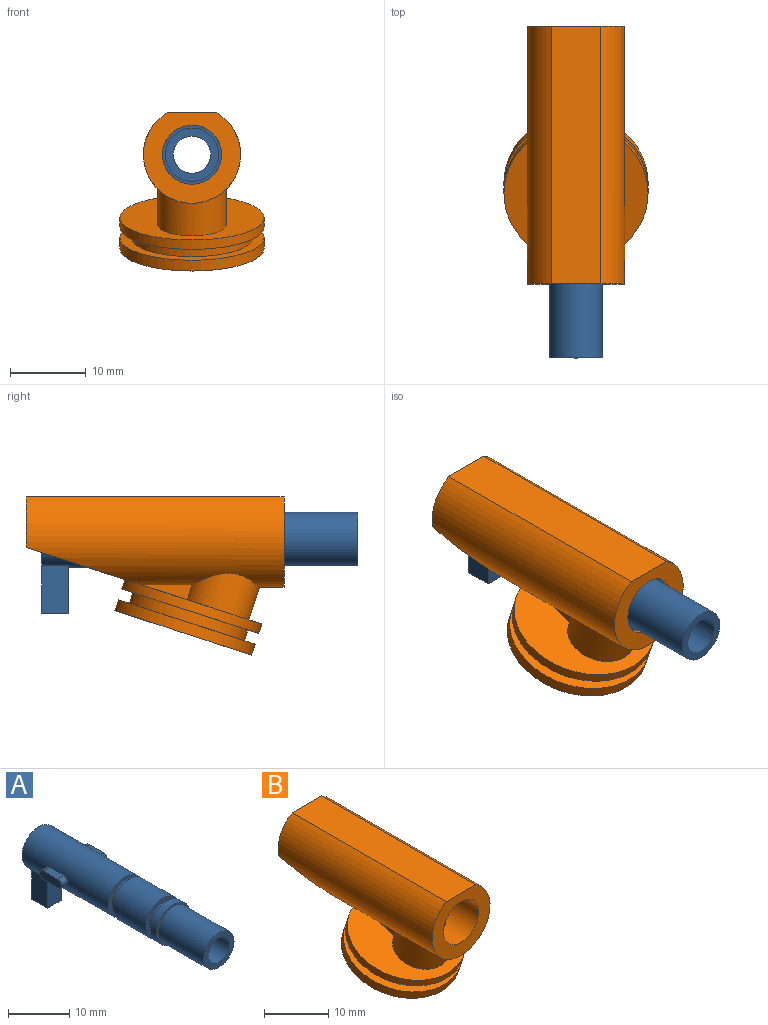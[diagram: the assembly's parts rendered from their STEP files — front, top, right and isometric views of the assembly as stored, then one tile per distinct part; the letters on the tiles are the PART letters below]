
ASSEMBLY  parts=2 mates=1
PART A: 32 faces, bbox 10.6x41.7x13.8 mm
  f0: plane 3.3x1.5mm, normal (0,0,1), area 4.9mm2, adj f2,f3,f4,f6
  f1: plane 3.3x1.5mm, normal (0,0,-1), area 4.9mm2, adj f2,f3,f4,f6
  f2: plane 5x1.7mm, normal (-1,0,0), area 7.9mm2, adj f0,f1,f3,f4
  f3: cylinder r=0.85mm len=1.7mm, axis (-1,0,0), area 3.9mm2, adj f0,f1,f2,f6
  f4: cylinder r=0.85mm len=1.7mm, axis (-1,0,0), area 3.9mm2, adj f0,f1,f2,f6
  f5: cylinder r=3.9mm len=7.8mm, axis (0,1,0), area 161.5mm2, adj f12,f13,f23,f24,f25,f26
  f6: cylinder r=3.9mm len=20mm, axis (0,1,0), area 462.3mm2, adj f0,f1,f3,f4,f9,f10,f19,f21
  f7: plane 7x7mm, normal (0,-1,0), area 19.6mm2, adj f8,f18
  f8: cylinder r=2.45mm len=41.7mm, axis (0,1,0), area 604.9mm2, adj f7,f9,f23,f24,f25,f26
  f9: plane 13.76x7.8mm, normal (0,1,0), area 48.3mm2, adj f6,f8,f19,f20,f21
  f10: plane 7.8x7.8mm, normal (0,-1,0), area 17.6mm2, adj f6,f11
  f11: cylinder r=3.1mm len=6.2mm, axis (0,1,0), area 19.5mm2, adj f10,f12
  f12: plane 7.8x7.8mm, normal (0,1,0), area 17.6mm2, adj f5,f11
  f13: plane 7.8x7.8mm, normal (0,-1,0), area 17.6mm2, adj f5,f14
  f14: cylinder r=3.1mm len=6.2mm, axis (0,1,0), area 19.5mm2, adj f13,f15
  f15: plane 7.8x7.8mm, normal (0,1,0), area 17.6mm2, adj f14,f16
  f16: cylinder r=3.9mm len=7.8mm, axis (0,1,0), area 36.8mm2, adj f15,f17
  f17: plane 7.8x7.8mm, normal (0,-1,0), area 9.3mm2, adj f16,f18
  f18: cylinder r=3.5mm len=10.5mm, axis (0,1,0), area 230.9mm2, adj f7,f17
  f19: plane 6.3x3.6mm, normal (1,0,0), area 22.7mm2, adj f6,f9,f20,f22
  f20: plane 3.6x3.2mm, normal (0,0,-1), area 11.5mm2, adj f9,f19,f21,f22
  f21: plane 6.3x3.6mm, normal (-1,0,0), area 22.7mm2, adj f6,f9,f20,f22
  f22: plane 6.3x3.2mm, normal (0,-1,0), area 19.4mm2, adj f6,f19,f20,f21
  f23: plane 4.9x3.9mm, normal (0,1,0), area 8.3mm2, adj f5,f8,f24,f26
  f24: plane 3.25x3.03mm, normal (-1,0,0), area 9.9mm2, adj f5,f8,f23,f25
  f25: cylinder r=2.45mm len=4.9mm, axis (0,0,-1), area 14.8mm2, adj f5,f8,f24,f26
  f26: plane 3.25x3.03mm, normal (1,0,0), area 9.9mm2, adj f5,f8,f23,f25
  f27: plane 3.3x1.5mm, normal (0,0,1), area 4.9mm2, adj f6,f29,f30,f31
  f28: plane 3.3x1.5mm, normal (0,0,-1), area 4.9mm2, adj f6,f29,f30,f31
  f29: plane 5x1.7mm, normal (1,0,0), area 7.9mm2, adj f27,f28,f30,f31
  f30: cylinder r=0.85mm len=1.7mm, axis (1,0,0), area 3.9mm2, adj f6,f27,f28,f29
  f31: cylinder r=0.85mm len=1.7mm, axis (1,0,0), area 3.9mm2, adj f6,f27,f28,f29
PART B: 26 faces, bbox 19.2x34.3x21 mm
  f0: plane 19.19x17.73mm, normal (0,-0.31,0.95), area 183.9mm2, adj f1,f2,f4,f20,f25
  f1: cylinder r=4.5mm len=9.73mm, axis (0,-0.31,0.95), area 105.4mm2, adj f0,f2,f20,f25
  f2: cylinder r=6.4mm len=34mm, axis (0,-1,0), area 853.6mm2, adj f0,f1,f11,f12,f18,f19,f20,f25
  f3: plane 19x18.07mm, normal (0,0.31,-0.95), area 263.9mm2, adj f8,f10
  f4: cylinder r=9.5mm len=19mm, axis (0,-0.31,0.95), area 77.6mm2, adj f0,f5,f18
  f5: plane 19x18.07mm, normal (0,0.31,-0.95), area 82.5mm2, adj f4,f6
  f6: cylinder r=8mm len=16mm, axis (0,-0.31,0.95), area 75.4mm2, adj f5,f7
  f7: plane 19x18.07mm, normal (0,-0.31,0.95), area 82.5mm2, adj f6,f8
  f8: cylinder r=9.5mm len=19mm, axis (0,-0.31,0.95), area 89.5mm2, adj f3,f7
  f9: cylinder r=3.9mm len=34mm, axis (0,-1,0), area 698.5mm2, adj f10,f11,f13,f15,f16,f17,f19,f21
  f10: cylinder r=2.5mm len=11.81mm, axis (0,-0.31,0.95), area 157.2mm2, adj f3,f9
  f11: plane 12.8x11.9mm, normal (0,-1,0), area 76.9mm2, adj f2,f9,f12
  f12: plane 34x6.55mm, normal (0,0,1), area 222.5mm2, adj f2,f11,f19
  f13: cylinder r=0.85mm len=1.7mm, axis (-1,0,0), area 3.9mm2, adj f9,f14,f15,f16
  f14: plane 12.5x1.7mm, normal (-1,0,0), area 20.9mm2, adj f13,f15,f16,f19
  f15: plane 11.65x1.5mm, normal (0,0,-1), area 17.5mm2, adj f9,f13,f14,f19
  f16: plane 11.65x1.5mm, normal (0,0,1), area 17.5mm2, adj f9,f13,f14,f17,f19
  f17: bspline ~10.42x8.23mm, area 16mm2, adj f9,f16,f18,f19,f24
  f18: plane 13.52x12.59mm, normal (0,0.31,-0.95), area 80.1mm2, adj f2,f4,f17,f19
  f19: plane 12.8x6.65mm, normal (0,1,0), area 37.3mm2, adj f2,f9,f12,f14,f15,f16,f17,f18
  f20: plane 6.73x1.98mm, normal (1,0,0), area 6.7mm2, adj f0,f1,f2
  f21: cylinder r=0.85mm len=1.7mm, axis (1,0,0), area 3.9mm2, adj f9,f22,f23,f24
  f22: plane 12.5x1.7mm, normal (1,0,0), area 20.9mm2, adj f19,f21,f23,f24
  f23: plane 11.65x1.5mm, normal (0,0,-1), area 17.5mm2, adj f9,f19,f21,f22
  f24: plane 11.65x1.5mm, normal (0,0,1), area 17.5mm2, adj f9,f17,f19,f21,f22
  f25: plane 6.73x1.98mm, normal (-1,0,0), area 6.7mm2, adj f0,f1,f2
PLACE A t=(0,-0.04,0)mm
PLACE B at identity fixed
MATE slider A.f5 <-> B.f2  axis (0,1,0) through (0,41.66,0)mm
